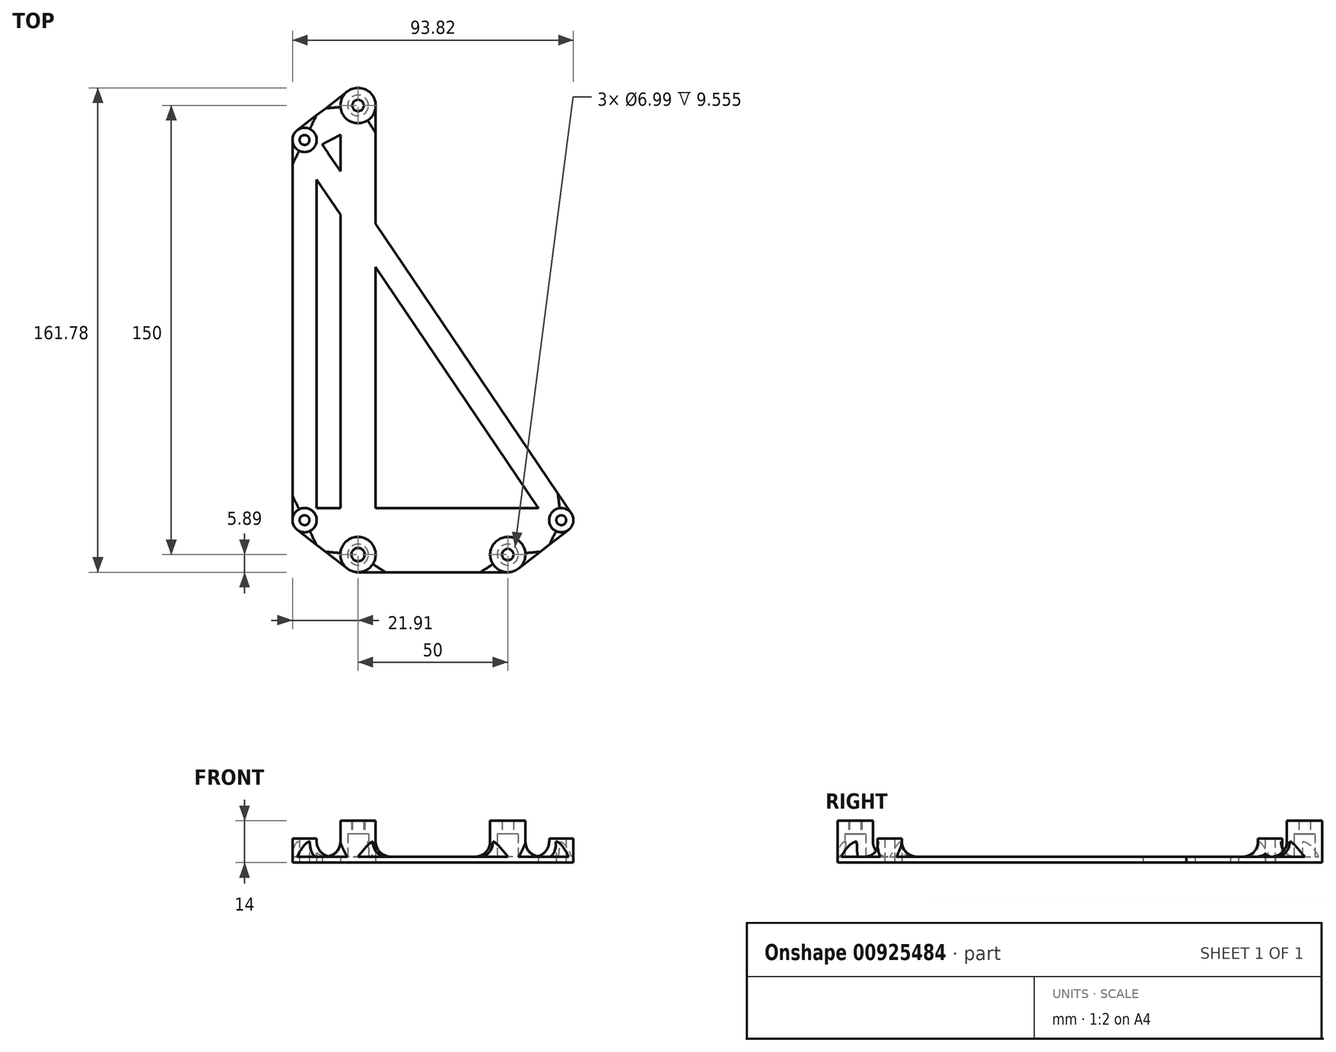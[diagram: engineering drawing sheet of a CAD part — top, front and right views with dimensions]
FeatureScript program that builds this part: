
annotation { "Feature Type Name" : "Feature", "Feature Type Description" : "" }
export const myFeature = defineFeature(function(context is Context, id is Id, definition is map)
    precondition{}
    {
        {
            var Q0;
            Q0=qCreatedBy(makeId("Top.planeOp"),FACE);
            var sketch = newSketch(context, id + "F0", { "sketchPlane" : qUnion([Q0])});
            skLineSegment(sketch, "E0.bottom", {"start": v(42.86, 63.5) * mm, "end": v(-42.86, 63.5) * mm, "construction": true});
            skLineSegment(sketch, "E0.top", {"start": v(42.86, -63.5) * mm, "end": v(-42.86, -63.5) * mm, "construction": true});
            skLineSegment(sketch, "E0.left", {"start": v(42.86, 63.5) * mm, "end": v(42.86, -63.5) * mm, "construction": true});
            skLineSegment(sketch, "E0.right", {"start": v(-42.86, 63.5) * mm, "end": v(-42.86, -63.5) * mm, "construction": true});
            skPoint(sketch, "E0.middle", {"position": v(0, 0) * mm});
            skPoint(sketch, "E1.MirrorP", {"position": v(85.73, 0) * mm});
            skCircle(sketch, "E2", {"center": v(-42.86, 63.5) * mm, "radius": 1.65 * mm});
            skCircle(sketch, "E3", {"center": v(-42.86, -63.5) * mm, "radius": 1.65 * mm});
            skCircle(sketch, "E4", {"center": v(42.86, -63.5) * mm, "radius": 1.65 * mm});
            skCircle(sketch, "E5", {"center": v(-42.86, 63.5) * mm, "radius": 4.05 * mm});
            skCircle(sketch, "E6", {"center": v(-42.86, -63.5) * mm, "radius": 4.05 * mm});
            skCircle(sketch, "E7", {"center": v(42.86, -63.5) * mm, "radius": 4.05 * mm});
            skLineSegment(sketch, "E8.bottom", {"start": v(-25, 75) * mm, "end": v(25, 75) * mm, "construction": true});
            skLineSegment(sketch, "E8.top", {"start": v(-25, -75) * mm, "end": v(25, -75) * mm, "construction": true});
            skLineSegment(sketch, "E8.left", {"start": v(-25, 75) * mm, "end": v(-25, -75) * mm, "construction": true});
            skLineSegment(sketch, "E8.right", {"start": v(25, 75) * mm, "end": v(25, -75) * mm, "construction": true});
            skLineSegment(sketch, "E9", {"start": v(-39.5, 65.77) * mm, "end": v(46.22, -61.23) * mm});
            skLineSegment(sketch, "E10", {"start": v(39.5, -65.77) * mm, "end": v(-46.22, 61.23) * mm});
            skLineSegment(sketch, "E11", {"start": v(-46.91, -63.5) * mm, "end": v(-46.91, 63.5) * mm});
            skLineSegment(sketch, "E12", {"start": v(-38.81, -63.5) * mm, "end": v(-38.81, 63.5) * mm});
            skLineSegment(sketch, "E13", {"start": v(-42.86, -59.45) * mm, "end": v(42.86, -59.45) * mm});
            skLineSegment(sketch, "E14", {"start": v(-42.86, -67.55) * mm, "end": v(42.86, -67.55) * mm});
            skCircle(sketch, "E15", {"center": v(-25, 75) * mm, "radius": 1.9 * mm});
            skCircle(sketch, "E16", {"center": v(-25, 75) * mm, "radius": 3.5 * mm});
            skCircle(sketch, "E17", {"center": v(-25, 75) * mm, "radius": 5.9 * mm});
            skLineSegment(sketch, "E18", {"start": v(-45.34, 66.7) * mm, "end": v(-28.6, 79.66) * mm});
            skLineSegment(sketch, "E19", {"start": v(-22.25, 69.79) * mm, "end": v(-40.97, 59.92) * mm});
            skCircle(sketch, "E20", {"center": v(-25, -75) * mm, "radius": 2.22 * mm});
            skCircle(sketch, "E21", {"center": v(-25, -75) * mm, "radius": 3.5 * mm});
            skCircle(sketch, "E22", {"center": v(-25, -75) * mm, "radius": 5.9 * mm});
            skCircle(sketch, "E23", {"center": v(25, -75) * mm, "radius": 1.9 * mm});
            skCircle(sketch, "E24", {"center": v(25, -75) * mm, "radius": 3.5 * mm});
            skCircle(sketch, "E25", {"center": v(25, -75) * mm, "radius": 5.9 * mm});
            skLineSegment(sketch, "E26", {"start": v(-45.34, -66.7) * mm, "end": v(-28.6, -79.66) * mm});
            skLineSegment(sketch, "E27", {"start": v(-22.25, -69.79) * mm, "end": v(-40.97, -59.92) * mm});
            skLineSegment(sketch, "E28", {"start": v(40.97, -59.92) * mm, "end": v(22.25, -69.79) * mm});
            skLineSegment(sketch, "E29", {"start": v(28.6, -79.66) * mm, "end": v(45.34, -66.7) * mm});
            skLineSegment(sketch, "E30", {"start": v(-25, -69.1) * mm, "end": v(25, -69.1) * mm});
            skLineSegment(sketch, "E31", {"start": v(25, -80.9) * mm, "end": v(-25, -80.9) * mm});
            skLineSegment(sketch, "E32", {"start": v(-30.9, 75) * mm, "end": v(-30.9, -75) * mm});
            skLineSegment(sketch, "E33", {"start": v(-19.1, -75) * mm, "end": v(-19.1, 75) * mm});
            skSolve(sketch);
        }
        {
            var Q0;
            {var subQ0=sQuery(id+"F0.wireOp",EDGE,"E18");Q0=makeQuery(id+"F0.imprint","IMPRINT",FACE,{"disambiguationData":[TD([[makeQuery(id+"F0.imprint","IMPRINT",EDGE,{"derivedFrom":subQ0}),-1.0]])]});}
            var Q1;
            {var subQ1=sQuery(id+"F0.wireOp",EDGE,"E9");var subQ5=sQuery(id+"F0.wireOp",EDGE,"E33");var subQ6=makeQuery(id+"F0.imprint","INTERSECT",VERTEX,{"derivedFrom":[subQ1,subQ5]});Q1=makeQuery(id+"F0.imprint","IMPRINT",FACE,{"disambiguationData":[TD([[makeQuery(id+"F0.imprint","IMPRINT",EDGE,{"disambiguationData":[TD([[subQ6,1.0]])],"derivedFrom":subQ1}),1.0]])]});}
            var Q2;
            {var subQ0=sQuery(id+"F0.wireOp",EDGE,"E19");var subQ1=sQuery(id+"F0.wireOp",EDGE,"E17");var subQ2=makeQuery(id+"F0.imprint","INTERSECT",VERTEX,{"derivedFrom":[subQ1,subQ0]});Q2=makeQuery(id+"F0.imprint","IMPRINT",FACE,{"disambiguationData":[TD([[makeQuery(id+"F0.imprint","IMPRINT",EDGE,{"disambiguationData":[TD([[subQ2,1.0]])],"derivedFrom":subQ1}),-1.0]])]});}
            var Q3;
            Q3=makeQuery(id+"F0.imprint","IMPRINT",FACE,{"disambiguationData":[TD([[makeQuery(id+"F0.imprint","IMPRINT",EDGE,{"derivedFrom":sQuery(id+"F0.wireOp",EDGE,"E16")}),-1.0]])]});
            var Q4;
            Q4=makeQuery(id+"F0.imprint","IMPRINT",FACE,{"disambiguationData":[TD([[makeQuery(id+"F0.imprint","IMPRINT",EDGE,{"derivedFrom":sQuery(id+"F0.wireOp",EDGE,"E15")}),-1.0]])]});
            var Q5;
            {var subQ0=sQuery(id+"F0.wireOp",EDGE,"E19");var subQ1=sQuery(id+"F0.wireOp",EDGE,"E9");var subQ2=makeQuery(id+"F0.imprint","INTERSECT",VERTEX,{"derivedFrom":[subQ1,subQ0]});Q5=makeQuery(id+"F0.imprint","IMPRINT",FACE,{"disambiguationData":[TD([[makeQuery(id+"F0.imprint","IMPRINT",EDGE,{"disambiguationData":[TD([[subQ2,-1.0]])],"derivedFrom":subQ1}),-1.0]])]});}
            var Q6;
            {var subQ0=sQuery(id+"F0.wireOp",EDGE,"E10");var subQ1=sQuery(id+"F0.wireOp",EDGE,"E5");var subQ2=makeQuery(id+"F0.imprint","INTERSECT",VERTEX,{"derivedFrom":[subQ1,subQ0]});Q6=makeQuery(id+"F0.imprint","IMPRINT",FACE,{"disambiguationData":[TD([[makeQuery(id+"F0.imprint","IMPRINT",EDGE,{"disambiguationData":[TD([[subQ2,-1.0]])],"derivedFrom":subQ1}),-1.0]])]});}
            var Q7;
            Q7=makeQuery(id+"F0.imprint","IMPRINT",FACE,{"disambiguationData":[TD([[makeQuery(id+"F0.imprint","IMPRINT",EDGE,{"derivedFrom":sQuery(id+"F0.wireOp",EDGE,"E2")}),-1.0]])]});
            var Q8;
            {var subQ0=sQuery(id+"F0.wireOp",EDGE,"E12");var subQ1=sQuery(id+"F0.wireOp",EDGE,"E5");var subQ2=makeQuery(id+"F0.imprint","INTERSECT",VERTEX,{"derivedFrom":[subQ1,subQ0]});Q8=makeQuery(id+"F0.imprint","IMPRINT",FACE,{"disambiguationData":[TD([[makeQuery(id+"F0.imprint","IMPRINT",EDGE,{"disambiguationData":[TD([[subQ2,1.0]])],"derivedFrom":subQ1}),-1.0]])]});}
            var Q9;
            {var subQ0=sQuery(id+"F0.wireOp",EDGE,"E9");var subQ1=sQuery(id+"F0.wireOp",EDGE,"E5");var subQ2=makeQuery(id+"F0.imprint","INTERSECT",VERTEX,{"derivedFrom":[subQ1,subQ0]});Q9=makeQuery(id+"F0.imprint","IMPRINT",FACE,{"disambiguationData":[TD([[makeQuery(id+"F0.imprint","IMPRINT",EDGE,{"disambiguationData":[TD([[subQ2,1.0]])],"derivedFrom":subQ1}),-1.0]])]});}
            var Q10;
            {var subQ0=sQuery(id+"F0.wireOp",EDGE,"E33");var subQ1=sQuery(id+"F0.wireOp",EDGE,"E9");var subQ2=makeQuery(id+"F0.imprint","INTERSECT",VERTEX,{"derivedFrom":[subQ1,subQ0]});Q10=makeQuery(id+"F0.imprint","IMPRINT",FACE,{"disambiguationData":[TD([[makeQuery(id+"F0.imprint","IMPRINT",EDGE,{"disambiguationData":[TD([[subQ2,1.0]])],"derivedFrom":subQ1}),-1.0]])]});}
            var Q11;
            {var subQ1=sQuery(id+"F0.wireOp",EDGE,"E7");var subQ7=sQuery(id+"F0.wireOp",EDGE,"E9");var subQ8=makeQuery(id+"F0.imprint","INTERSECT",VERTEX,{"derivedFrom":[subQ1,subQ7]});Q11=makeQuery(id+"F0.imprint","IMPRINT",FACE,{"disambiguationData":[TD([[makeQuery(id+"F0.imprint","IMPRINT",EDGE,{"disambiguationData":[TD([[subQ8,-1.0]])],"derivedFrom":subQ1}),-1.0]])]});}
            var Q12;
            {var subQ0=sQuery(id+"F0.wireOp",EDGE,"E33");var subQ1=sQuery(id+"F0.wireOp",EDGE,"E10");var subQ2=makeQuery(id+"F0.imprint","INTERSECT",VERTEX,{"derivedFrom":[subQ1,subQ0]});Q12=makeQuery(id+"F0.imprint","IMPRINT",FACE,{"disambiguationData":[TD([[makeQuery(id+"F0.imprint","IMPRINT",EDGE,{"disambiguationData":[TD([[subQ2,-1.0]])],"derivedFrom":subQ1}),1.0]])]});}
            var Q13;
            {var subQ5=sQuery(id+"F0.wireOp",EDGE,"E11");Q13=makeQuery(id+"F0.imprint","IMPRINT",FACE,{"disambiguationData":[TD([[makeQuery(id+"F0.imprint","IMPRINT",EDGE,{"derivedFrom":subQ5}),-1.0]])]});}
            var Q14;
            {var subQ0=sQuery(id+"F0.wireOp",EDGE,"E13");var subQ1=sQuery(id+"F0.wireOp",EDGE,"E6");var subQ2=makeQuery(id+"F0.imprint","INTERSECT",VERTEX,{"derivedFrom":[subQ1,subQ0]});Q14=makeQuery(id+"F0.imprint","IMPRINT",FACE,{"disambiguationData":[TD([[makeQuery(id+"F0.imprint","IMPRINT",EDGE,{"disambiguationData":[TD([[subQ2,1.0]])],"derivedFrom":subQ1}),-1.0]])]});}
            var Q15;
            {var subQ0=sQuery(id+"F0.wireOp",EDGE,"E12");var subQ1=sQuery(id+"F0.wireOp",EDGE,"E6");var subQ2=makeQuery(id+"F0.imprint","INTERSECT",VERTEX,{"derivedFrom":[subQ1,subQ0]});Q15=makeQuery(id+"F0.imprint","IMPRINT",FACE,{"disambiguationData":[TD([[makeQuery(id+"F0.imprint","IMPRINT",EDGE,{"disambiguationData":[TD([[subQ2,-1.0]])],"derivedFrom":subQ1}),-1.0]])]});}
            var Q16;
            Q16=makeQuery(id+"F0.imprint","IMPRINT",FACE,{"disambiguationData":[TD([[makeQuery(id+"F0.imprint","IMPRINT",EDGE,{"derivedFrom":sQuery(id+"F0.wireOp",EDGE,"E3")}),-1.0]])]});
            var Q17;
            {var subQ0=sQuery(id+"F0.wireOp",EDGE,"E27");var subQ1=sQuery(id+"F0.wireOp",EDGE,"E12");var subQ2=makeQuery(id+"F0.imprint","INTERSECT",VERTEX,{"derivedFrom":[subQ1,subQ0]});Q17=makeQuery(id+"F0.imprint","IMPRINT",FACE,{"disambiguationData":[TD([[makeQuery(id+"F0.imprint","IMPRINT",EDGE,{"disambiguationData":[TD([[subQ2,-1.0]])],"derivedFrom":subQ1}),-1.0]])]});}
            var Q18;
            {var subQ1=sQuery(id+"F0.wireOp",EDGE,"E12");var subQ5=sQuery(id+"F0.wireOp",EDGE,"E6");var subQ6=makeQuery(id+"F0.imprint","INTERSECT",VERTEX,{"derivedFrom":[subQ5,subQ1]});Q18=makeQuery(id+"F0.imprint","IMPRINT",FACE,{"disambiguationData":[TD([[makeQuery(id+"F0.imprint","IMPRINT",EDGE,{"disambiguationData":[TD([[subQ6,1.0]])],"derivedFrom":subQ5}),-1.0]])]});}
            var Q19;
            {var subQ0=sQuery(id+"F0.wireOp",EDGE,"E32");var subQ1=sQuery(id+"F0.wireOp",EDGE,"E13");var subQ2=makeQuery(id+"F0.imprint","INTERSECT",VERTEX,{"derivedFrom":[subQ1,subQ0]});Q19=makeQuery(id+"F0.imprint","IMPRINT",FACE,{"disambiguationData":[TD([[makeQuery(id+"F0.imprint","IMPRINT",EDGE,{"disambiguationData":[TD([[subQ2,-1.0]])],"derivedFrom":subQ1}),-1.0]])]});}
            var Q20;
            {var subQ0=sQuery(id+"F0.wireOp",EDGE,"E32");var subQ1=sQuery(id+"F0.wireOp",EDGE,"E14");var subQ2=makeQuery(id+"F0.imprint","INTERSECT",VERTEX,{"derivedFrom":[subQ1,subQ0]});Q20=makeQuery(id+"F0.imprint","IMPRINT",FACE,{"disambiguationData":[TD([[makeQuery(id+"F0.imprint","IMPRINT",EDGE,{"disambiguationData":[TD([[subQ2,-1.0]])],"derivedFrom":subQ1}),1.0]])]});}
            var Q21;
            {var subQ1=sQuery(id+"F0.wireOp",EDGE,"E14");var subQ7=sQuery(id+"F0.wireOp",EDGE,"E32");var subQ9=makeQuery(id+"F0.imprint","INTERSECT",VERTEX,{"derivedFrom":[subQ1,subQ7]});Q21=makeQuery(id+"F0.imprint","IMPRINT",FACE,{"disambiguationData":[TD([[makeQuery(id+"F0.imprint","IMPRINT",EDGE,{"disambiguationData":[TD([[subQ9,-1.0]])],"derivedFrom":subQ1}),-1.0]])]});}
            var Q22;
            {var subQ0=sQuery(id+"F0.wireOp",EDGE,"E26");Q22=makeQuery(id+"F0.imprint","IMPRINT",FACE,{"disambiguationData":[TD([[makeQuery(id+"F0.imprint","IMPRINT",EDGE,{"derivedFrom":subQ0}),1.0]])]});}
            var Q23;
            {var subQ0=sQuery(id+"F0.wireOp",EDGE,"E27");var subQ1=sQuery(id+"F0.wireOp",EDGE,"E14");var subQ2=makeQuery(id+"F0.imprint","INTERSECT",VERTEX,{"derivedFrom":[subQ1,subQ0]});Q23=makeQuery(id+"F0.imprint","IMPRINT",FACE,{"disambiguationData":[TD([[makeQuery(id+"F0.imprint","IMPRINT",EDGE,{"disambiguationData":[TD([[subQ2,-1.0]])],"derivedFrom":subQ1}),-1.0]])]});}
            var Q24;
            {var subQ0=sQuery(id+"F0.wireOp",EDGE,"E27");var subQ1=sQuery(id+"F0.wireOp",EDGE,"E22");var subQ2=makeQuery(id+"F0.imprint","INTERSECT",VERTEX,{"derivedFrom":[subQ1,subQ0]});Q24=makeQuery(id+"F0.imprint","IMPRINT",FACE,{"disambiguationData":[TD([[makeQuery(id+"F0.imprint","IMPRINT",EDGE,{"disambiguationData":[TD([[subQ2,-1.0]])],"derivedFrom":subQ1}),-1.0]])]});}
            var Q25;
            {var subQ0=sQuery(id+"F0.wireOp",EDGE,"E27");var subQ1=sQuery(id+"F0.wireOp",EDGE,"E22");var subQ2=makeQuery(id+"F0.imprint","INTERSECT",VERTEX,{"derivedFrom":[subQ1,subQ0]});Q25=makeQuery(id+"F0.imprint","IMPRINT",FACE,{"disambiguationData":[TD([[makeQuery(id+"F0.imprint","IMPRINT",EDGE,{"disambiguationData":[TD([[subQ2,1.0]])],"derivedFrom":subQ1}),-1.0]])]});}
            var Q26;
            Q26=makeQuery(id+"F0.imprint","IMPRINT",FACE,{"disambiguationData":[TD([[makeQuery(id+"F0.imprint","IMPRINT",EDGE,{"derivedFrom":sQuery(id+"F0.wireOp",EDGE,"E21")}),-1.0]])]});
            var Q27;
            Q27=makeQuery(id+"F0.imprint","IMPRINT",FACE,{"disambiguationData":[TD([[makeQuery(id+"F0.imprint","IMPRINT",EDGE,{"derivedFrom":sQuery(id+"F0.wireOp",EDGE,"E20")}),-1.0]])]});
            var Q28;
            {var subQ5=sQuery(id+"F0.wireOp",EDGE,"E31");Q28=makeQuery(id+"F0.imprint","IMPRINT",FACE,{"disambiguationData":[TD([[makeQuery(id+"F0.imprint","IMPRINT",EDGE,{"derivedFrom":subQ5}),-1.0]])]});}
            var Q29;
            {var subQ0=sQuery(id+"F0.wireOp",EDGE,"E13");var subQ1=sQuery(id+"F0.wireOp",EDGE,"E7");var subQ2=makeQuery(id+"F0.imprint","INTERSECT",VERTEX,{"derivedFrom":[subQ1,subQ0]});Q29=makeQuery(id+"F0.imprint","IMPRINT",FACE,{"disambiguationData":[TD([[makeQuery(id+"F0.imprint","IMPRINT",EDGE,{"disambiguationData":[TD([[subQ2,-1.0]])],"derivedFrom":subQ1}),-1.0]])]});}
            var Q30;
            {var subQ0=sQuery(id+"F0.wireOp",EDGE,"E10");var subQ1=sQuery(id+"F0.wireOp",EDGE,"E7");var subQ2=makeQuery(id+"F0.imprint","INTERSECT",VERTEX,{"derivedFrom":[subQ1,subQ0]});Q30=makeQuery(id+"F0.imprint","IMPRINT",FACE,{"disambiguationData":[TD([[makeQuery(id+"F0.imprint","IMPRINT",EDGE,{"disambiguationData":[TD([[subQ2,1.0]])],"derivedFrom":subQ1}),-1.0]])]});}
            var Q31;
            Q31=makeQuery(id+"F0.imprint","IMPRINT",FACE,{"disambiguationData":[TD([[makeQuery(id+"F0.imprint","IMPRINT",EDGE,{"derivedFrom":sQuery(id+"F0.wireOp",EDGE,"E4")}),-1.0]])]});
            var Q32;
            {var subQ0=sQuery(id+"F0.wireOp",EDGE,"E10");var subQ1=sQuery(id+"F0.wireOp",EDGE,"E7");var subQ2=makeQuery(id+"F0.imprint","INTERSECT",VERTEX,{"derivedFrom":[subQ1,subQ0]});Q32=makeQuery(id+"F0.imprint","IMPRINT",FACE,{"disambiguationData":[TD([[makeQuery(id+"F0.imprint","IMPRINT",EDGE,{"disambiguationData":[TD([[subQ2,-1.0]])],"derivedFrom":subQ1}),-1.0]])]});}
            var Q33;
            {var subQ5=sQuery(id+"F0.wireOp",EDGE,"E29");Q33=makeQuery(id+"F0.imprint","IMPRINT",FACE,{"disambiguationData":[TD([[makeQuery(id+"F0.imprint","IMPRINT",EDGE,{"derivedFrom":subQ5}),1.0]])]});}
            var Q34;
            {var subQ0=sQuery(id+"F0.wireOp",EDGE,"E28");var subQ1=sQuery(id+"F0.wireOp",EDGE,"E25");var subQ2=makeQuery(id+"F0.imprint","INTERSECT",VERTEX,{"derivedFrom":[subQ1,subQ0]});Q34=makeQuery(id+"F0.imprint","IMPRINT",FACE,{"disambiguationData":[TD([[makeQuery(id+"F0.imprint","IMPRINT",EDGE,{"disambiguationData":[TD([[subQ2,1.0]])],"derivedFrom":subQ1}),-1.0]])]});}
            var Q35;
            Q35=makeQuery(id+"F0.imprint","IMPRINT",FACE,{"disambiguationData":[TD([[makeQuery(id+"F0.imprint","IMPRINT",EDGE,{"derivedFrom":sQuery(id+"F0.wireOp",EDGE,"E24")}),-1.0]])]});
            var Q36;
            Q36=makeQuery(id+"F0.imprint","IMPRINT",FACE,{"disambiguationData":[TD([[makeQuery(id+"F0.imprint","IMPRINT",EDGE,{"derivedFrom":sQuery(id+"F0.wireOp",EDGE,"E23")}),-1.0]])]});
            var Q37;
            {var subQ0=sQuery(id+"F0.wireOp",EDGE,"E28");var subQ1=sQuery(id+"F0.wireOp",EDGE,"E10");var subQ2=makeQuery(id+"F0.imprint","INTERSECT",VERTEX,{"derivedFrom":[subQ1,subQ0]});Q37=makeQuery(id+"F0.imprint","IMPRINT",FACE,{"disambiguationData":[TD([[makeQuery(id+"F0.imprint","IMPRINT",EDGE,{"disambiguationData":[TD([[subQ2,-1.0]])],"derivedFrom":subQ1}),1.0]])]});}
            var Q38;
            {var subQ0=sQuery(id+"F0.wireOp",EDGE,"E33");var subQ1=sQuery(id+"F0.wireOp",EDGE,"E14");var subQ2=makeQuery(id+"F0.imprint","INTERSECT",VERTEX,{"derivedFrom":[subQ1,subQ0]});Q38=makeQuery(id+"F0.imprint","IMPRINT",FACE,{"disambiguationData":[TD([[makeQuery(id+"F0.imprint","IMPRINT",EDGE,{"disambiguationData":[TD([[subQ2,-1.0]])],"derivedFrom":subQ1}),-1.0]])]});}
            extrude(context, id + "F1", {"entities" : qUnion([Q0, Q1, Q2, Q3, Q4, Q5, Q6, Q7, Q8, Q9, Q10, Q11, Q12, Q13, Q14, Q15, Q16, Q17, Q18, Q19, Q20, Q21, Q22, Q23, Q24, Q25, Q26, Q27, Q28, Q29, Q30, Q31, Q32, Q33, Q34, Q35, Q36, Q37, Q38]), "depth" : 2 * mm, "offsetDistance" : 25.4 * mm});
        }
        {
            var Q0;
            Q0=makeQuery(id+"F0.imprint","IMPRINT",FACE,{"disambiguationData":[TD([[makeQuery(id+"F0.imprint","IMPRINT",EDGE,{"derivedFrom":sQuery(id+"F0.wireOp",EDGE,"E16")}),-1.0]])]});
            var Q1;
            Q1=makeQuery(id+"F0.imprint","IMPRINT",FACE,{"disambiguationData":[TD([[makeQuery(id+"F0.imprint","IMPRINT",EDGE,{"derivedFrom":sQuery(id+"F0.wireOp",EDGE,"E15")}),-1.0]])]});
            var Q2;
            Q2=makeQuery(id+"F0.imprint","IMPRINT",FACE,{"disambiguationData":[TD([[makeQuery(id+"F0.imprint","IMPRINT",EDGE,{"derivedFrom":sQuery(id+"F0.wireOp",EDGE,"E20")}),-1.0]])]});
            var Q3;
            Q3=makeQuery(id+"F0.imprint","IMPRINT",FACE,{"disambiguationData":[TD([[makeQuery(id+"F0.imprint","IMPRINT",EDGE,{"derivedFrom":sQuery(id+"F0.wireOp",EDGE,"E21")}),-1.0]])]});
            var Q4;
            Q4=makeQuery(id+"F0.imprint","IMPRINT",FACE,{"disambiguationData":[TD([[makeQuery(id+"F0.imprint","IMPRINT",EDGE,{"derivedFrom":sQuery(id+"F0.wireOp",EDGE,"E23")}),-1.0]])]});
            var Q5;
            Q5=makeQuery(id+"F0.imprint","IMPRINT",FACE,{"disambiguationData":[TD([[makeQuery(id+"F0.imprint","IMPRINT",EDGE,{"derivedFrom":sQuery(id+"F0.wireOp",EDGE,"E24")}),-1.0]])]});
            extrude(context, id + "F2", {"entities" : qUnion([Q0, Q1, Q2, Q3, Q4, Q5]), "operationType" : NewBodyOperationType.ADD, "depth" : 14 * mm, "offsetDistance" : 25.4 * mm});
        }
        {
            var Q0;
            Q0=makeQuery(id+"F0.imprint","IMPRINT",FACE,{"disambiguationData":[TD([[makeQuery(id+"F0.imprint","IMPRINT",EDGE,{"derivedFrom":sQuery(id+"F0.wireOp",EDGE,"E20")}),-1.0]])]});
            var Q1;
            Q1=makeQuery(id+"F0.imprint","IMPRINT",FACE,{"disambiguationData":[TD([[makeQuery(id+"F0.imprint","IMPRINT",EDGE,{"derivedFrom":sQuery(id+"F0.wireOp",EDGE,"E23")}),-1.0]])]});
            var Q2;
            Q2=makeQuery(id+"F0.imprint","IMPRINT",FACE,{"disambiguationData":[TD([[makeQuery(id+"F0.imprint","IMPRINT",EDGE,{"derivedFrom":sQuery(id+"F0.wireOp",EDGE,"E15")}),-1.0]])]});
            extrude(context, id + "F3", {"entities" : qUnion([Q0, Q1, Q2]), "operationType" : NewBodyOperationType.REMOVE, "depth" : 14 * mm - 4.44 * mm, "offsetDistance" : 25.4 * mm});
        }
        {
            var Q0;
            Q0=makeQuery(id+"F0.imprint","IMPRINT",FACE,{"disambiguationData":[TD([[makeQuery(id+"F0.imprint","IMPRINT",EDGE,{"derivedFrom":sQuery(id+"F0.wireOp",EDGE,"E3")}),-1.0]])]});
            var Q1;
            Q1=makeQuery(id+"F0.imprint","IMPRINT",FACE,{"disambiguationData":[TD([[makeQuery(id+"F0.imprint","IMPRINT",EDGE,{"derivedFrom":sQuery(id+"F0.wireOp",EDGE,"E4")}),-1.0]])]});
            var Q2;
            Q2=makeQuery(id+"F0.imprint","IMPRINT",FACE,{"disambiguationData":[TD([[makeQuery(id+"F0.imprint","IMPRINT",EDGE,{"derivedFrom":sQuery(id+"F0.wireOp",EDGE,"E2")}),-1.0]])]});
            extrude(context, id + "F4", {"entities" : qUnion([Q0, Q1, Q2]), "operationType" : NewBodyOperationType.ADD, "depth" : 8 * mm, "offsetDistance" : 25 * mm});
        }
        {
            var Q0;
            {var subQ0=sQuery(id+"F0.wireOp",EDGE,"E6");Q0=makeQuery(id+"F4.boolean.opBoolean","INTERSECT",EDGE,{"derivedFrom":[makeQuery(id+"F1.opExtrude","CAP_FACE",FACE,{"disambiguationData":[OSD([sQuery(id+"F0.wireOp",EDGE,"E2"),sQuery(id+"F0.wireOp",EDGE,"E3"),sQuery(id+"F0.wireOp",EDGE,"E4"),sQuery(id+"F0.wireOp",EDGE,"E5"),subQ0,sQuery(id+"F0.wireOp",EDGE,"E7"),sQuery(id+"F0.wireOp",EDGE,"E9"),sQuery(id+"F0.wireOp",EDGE,"E10"),sQuery(id+"F0.wireOp",EDGE,"E11"),sQuery(id+"F0.wireOp",EDGE,"E12"),sQuery(id+"F0.wireOp",EDGE,"E13"),sQuery(id+"F0.wireOp",EDGE,"E15"),sQuery(id+"F0.wireOp",EDGE,"E17"),sQuery(id+"F0.wireOp",EDGE,"E18"),sQuery(id+"F0.wireOp",EDGE,"E19"),sQuery(id+"F0.wireOp",EDGE,"E20"),sQuery(id+"F0.wireOp",EDGE,"E22"),sQuery(id+"F0.wireOp",EDGE,"E23"),sQuery(id+"F0.wireOp",EDGE,"E25"),sQuery(id+"F0.wireOp",EDGE,"E26"),sQuery(id+"F0.wireOp",EDGE,"E29"),sQuery(id+"F0.wireOp",EDGE,"E31"),sQuery(id+"F0.wireOp",EDGE,"E32"),sQuery(id+"F0.wireOp",EDGE,"E33")])],"isStart":false}),makeQuery(id+"F4.opExtrude","SWEPT_FACE",FACE,{"disambiguationData":[OSD([subQ0])]})]});}
            var Q1;
            {var subQ0=sQuery(id+"F0.wireOp",EDGE,"E22");Q1=makeQuery(id+"F2.boolean.opBoolean","INTERSECT",EDGE,{"derivedFrom":[makeQuery(id+"F1.opExtrude","CAP_FACE",FACE,{"disambiguationData":[OSD([sQuery(id+"F0.wireOp",EDGE,"E2"),sQuery(id+"F0.wireOp",EDGE,"E3"),sQuery(id+"F0.wireOp",EDGE,"E4"),sQuery(id+"F0.wireOp",EDGE,"E5"),sQuery(id+"F0.wireOp",EDGE,"E6"),sQuery(id+"F0.wireOp",EDGE,"E7"),sQuery(id+"F0.wireOp",EDGE,"E9"),sQuery(id+"F0.wireOp",EDGE,"E10"),sQuery(id+"F0.wireOp",EDGE,"E11"),sQuery(id+"F0.wireOp",EDGE,"E12"),sQuery(id+"F0.wireOp",EDGE,"E13"),sQuery(id+"F0.wireOp",EDGE,"E15"),sQuery(id+"F0.wireOp",EDGE,"E17"),sQuery(id+"F0.wireOp",EDGE,"E18"),sQuery(id+"F0.wireOp",EDGE,"E19"),sQuery(id+"F0.wireOp",EDGE,"E20"),subQ0,sQuery(id+"F0.wireOp",EDGE,"E23"),sQuery(id+"F0.wireOp",EDGE,"E25"),sQuery(id+"F0.wireOp",EDGE,"E26"),sQuery(id+"F0.wireOp",EDGE,"E29"),sQuery(id+"F0.wireOp",EDGE,"E31"),sQuery(id+"F0.wireOp",EDGE,"E32"),sQuery(id+"F0.wireOp",EDGE,"E33")])],"isStart":false}),makeQuery(id+"F2.opExtrude","SWEPT_FACE",FACE,{"disambiguationData":[OSD([subQ0])]})]});}
            var Q2;
            {var subQ0=sQuery(id+"F0.wireOp",EDGE,"E25");Q2=makeQuery(id+"F2.boolean.opBoolean","INTERSECT",EDGE,{"derivedFrom":[makeQuery(id+"F1.opExtrude","CAP_FACE",FACE,{"disambiguationData":[OSD([sQuery(id+"F0.wireOp",EDGE,"E2"),sQuery(id+"F0.wireOp",EDGE,"E3"),sQuery(id+"F0.wireOp",EDGE,"E4"),sQuery(id+"F0.wireOp",EDGE,"E5"),sQuery(id+"F0.wireOp",EDGE,"E6"),sQuery(id+"F0.wireOp",EDGE,"E7"),sQuery(id+"F0.wireOp",EDGE,"E9"),sQuery(id+"F0.wireOp",EDGE,"E10"),sQuery(id+"F0.wireOp",EDGE,"E11"),sQuery(id+"F0.wireOp",EDGE,"E12"),sQuery(id+"F0.wireOp",EDGE,"E13"),sQuery(id+"F0.wireOp",EDGE,"E15"),sQuery(id+"F0.wireOp",EDGE,"E17"),sQuery(id+"F0.wireOp",EDGE,"E18"),sQuery(id+"F0.wireOp",EDGE,"E19"),sQuery(id+"F0.wireOp",EDGE,"E20"),sQuery(id+"F0.wireOp",EDGE,"E22"),sQuery(id+"F0.wireOp",EDGE,"E23"),subQ0,sQuery(id+"F0.wireOp",EDGE,"E26"),sQuery(id+"F0.wireOp",EDGE,"E29"),sQuery(id+"F0.wireOp",EDGE,"E31"),sQuery(id+"F0.wireOp",EDGE,"E32"),sQuery(id+"F0.wireOp",EDGE,"E33")])],"isStart":false}),makeQuery(id+"F2.opExtrude","SWEPT_FACE",FACE,{"disambiguationData":[OSD([subQ0])]})]});}
            var Q3;
            {var subQ0=sQuery(id+"F0.wireOp",EDGE,"E7");Q3=makeQuery(id+"F4.boolean.opBoolean","INTERSECT",EDGE,{"derivedFrom":[makeQuery(id+"F1.opExtrude","CAP_FACE",FACE,{"disambiguationData":[OSD([sQuery(id+"F0.wireOp",EDGE,"E2"),sQuery(id+"F0.wireOp",EDGE,"E3"),sQuery(id+"F0.wireOp",EDGE,"E4"),sQuery(id+"F0.wireOp",EDGE,"E5"),sQuery(id+"F0.wireOp",EDGE,"E6"),subQ0,sQuery(id+"F0.wireOp",EDGE,"E9"),sQuery(id+"F0.wireOp",EDGE,"E10"),sQuery(id+"F0.wireOp",EDGE,"E11"),sQuery(id+"F0.wireOp",EDGE,"E12"),sQuery(id+"F0.wireOp",EDGE,"E13"),sQuery(id+"F0.wireOp",EDGE,"E15"),sQuery(id+"F0.wireOp",EDGE,"E17"),sQuery(id+"F0.wireOp",EDGE,"E18"),sQuery(id+"F0.wireOp",EDGE,"E19"),sQuery(id+"F0.wireOp",EDGE,"E20"),sQuery(id+"F0.wireOp",EDGE,"E22"),sQuery(id+"F0.wireOp",EDGE,"E23"),sQuery(id+"F0.wireOp",EDGE,"E25"),sQuery(id+"F0.wireOp",EDGE,"E26"),sQuery(id+"F0.wireOp",EDGE,"E29"),sQuery(id+"F0.wireOp",EDGE,"E31"),sQuery(id+"F0.wireOp",EDGE,"E32"),sQuery(id+"F0.wireOp",EDGE,"E33")])],"isStart":false}),makeQuery(id+"F4.opExtrude","SWEPT_FACE",FACE,{"disambiguationData":[OSD([subQ0])]})]});}
            var Q4;
            {var subQ0=sQuery(id+"F0.wireOp",EDGE,"E5");Q4=makeQuery(id+"F4.boolean.opBoolean","INTERSECT",EDGE,{"derivedFrom":[makeQuery(id+"F1.opExtrude","CAP_FACE",FACE,{"disambiguationData":[OSD([sQuery(id+"F0.wireOp",EDGE,"E2"),sQuery(id+"F0.wireOp",EDGE,"E3"),sQuery(id+"F0.wireOp",EDGE,"E4"),subQ0,sQuery(id+"F0.wireOp",EDGE,"E6"),sQuery(id+"F0.wireOp",EDGE,"E7"),sQuery(id+"F0.wireOp",EDGE,"E9"),sQuery(id+"F0.wireOp",EDGE,"E10"),sQuery(id+"F0.wireOp",EDGE,"E11"),sQuery(id+"F0.wireOp",EDGE,"E12"),sQuery(id+"F0.wireOp",EDGE,"E13"),sQuery(id+"F0.wireOp",EDGE,"E15"),sQuery(id+"F0.wireOp",EDGE,"E17"),sQuery(id+"F0.wireOp",EDGE,"E18"),sQuery(id+"F0.wireOp",EDGE,"E19"),sQuery(id+"F0.wireOp",EDGE,"E20"),sQuery(id+"F0.wireOp",EDGE,"E22"),sQuery(id+"F0.wireOp",EDGE,"E23"),sQuery(id+"F0.wireOp",EDGE,"E25"),sQuery(id+"F0.wireOp",EDGE,"E26"),sQuery(id+"F0.wireOp",EDGE,"E29"),sQuery(id+"F0.wireOp",EDGE,"E31"),sQuery(id+"F0.wireOp",EDGE,"E32"),sQuery(id+"F0.wireOp",EDGE,"E33")])],"isStart":false}),makeQuery(id+"F4.opExtrude","SWEPT_FACE",FACE,{"disambiguationData":[OSD([subQ0])]})]});}
            var Q5;
            {var subQ0=sQuery(id+"F0.wireOp",EDGE,"E17");Q5=makeQuery(id+"F2.boolean.opBoolean","INTERSECT",EDGE,{"derivedFrom":[makeQuery(id+"F1.opExtrude","CAP_FACE",FACE,{"disambiguationData":[OSD([sQuery(id+"F0.wireOp",EDGE,"E2"),sQuery(id+"F0.wireOp",EDGE,"E3"),sQuery(id+"F0.wireOp",EDGE,"E4"),sQuery(id+"F0.wireOp",EDGE,"E5"),sQuery(id+"F0.wireOp",EDGE,"E6"),sQuery(id+"F0.wireOp",EDGE,"E7"),sQuery(id+"F0.wireOp",EDGE,"E9"),sQuery(id+"F0.wireOp",EDGE,"E10"),sQuery(id+"F0.wireOp",EDGE,"E11"),sQuery(id+"F0.wireOp",EDGE,"E12"),sQuery(id+"F0.wireOp",EDGE,"E13"),sQuery(id+"F0.wireOp",EDGE,"E15"),subQ0,sQuery(id+"F0.wireOp",EDGE,"E18"),sQuery(id+"F0.wireOp",EDGE,"E19"),sQuery(id+"F0.wireOp",EDGE,"E20"),sQuery(id+"F0.wireOp",EDGE,"E22"),sQuery(id+"F0.wireOp",EDGE,"E23"),sQuery(id+"F0.wireOp",EDGE,"E25"),sQuery(id+"F0.wireOp",EDGE,"E26"),sQuery(id+"F0.wireOp",EDGE,"E29"),sQuery(id+"F0.wireOp",EDGE,"E31"),sQuery(id+"F0.wireOp",EDGE,"E32"),sQuery(id+"F0.wireOp",EDGE,"E33")])],"isStart":false}),makeQuery(id+"F2.opExtrude","SWEPT_FACE",FACE,{"disambiguationData":[OSD([subQ0])]})]});}
            fillet(context, id + "F5", {"entities" : qUnion([Q0, Q1, Q2, Q3, Q4, Q5]), "radius" : 5 * mm, "tangentPropagation" : true, "allowEdgeOverflow" : false});
        }
    });
